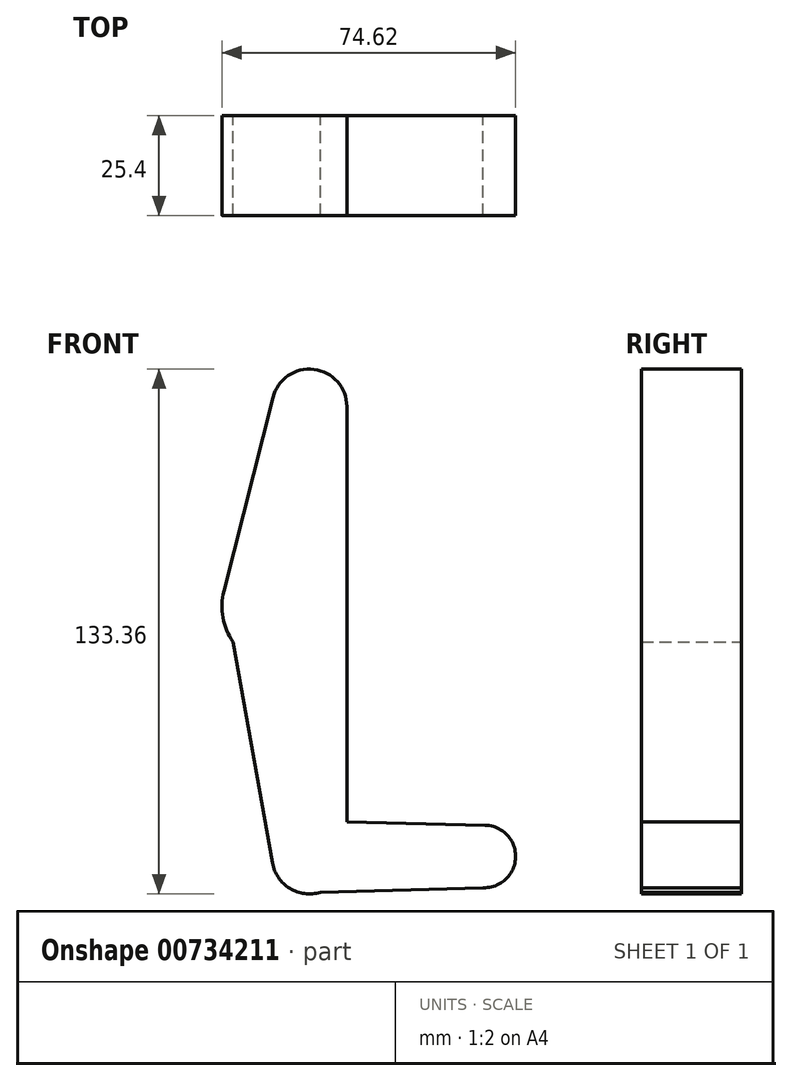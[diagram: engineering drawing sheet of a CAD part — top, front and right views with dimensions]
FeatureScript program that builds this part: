
annotation { "Feature Type Name" : "Feature", "Feature Type Description" : "" }
export const myFeature = defineFeature(function(context is Context, id is Id, definition is map)
    precondition{}
    {
        {
            var Q0;
            Q0=qCreatedBy(makeId("Front.planeOp"),FACE);
            var sketch = newSketch(context, id + "F0", { "sketchPlane" : qUnion([Q0])});
            skPoint(sketch, "E0.end.orphan", {"position": v(0, 1423.13) * mm});
            skLineSegment(sketch, "E1", {"start": v(0, 0) * mm, "end": v(44.45, 0) * mm});
            skCircle(sketch, "E2", {"center": v(0, 114.3) * mm, "radius": 9.53 * mm});
            skCircle(sketch, "E3", {"center": v(-6.35, 63.5) * mm, "radius": 15.88 * mm});
            skCircle(sketch, "E4", {"center": v(44.45, 0) * mm, "radius": 7.94 * mm});
            skCircle(sketch, "E5", {"center": v(0, 0) * mm, "radius": 9.53 * mm});
            skLineSegment(sketch, "E6", {"start": v(0, 114.3) * mm, "end": v(0, 0) * mm, "construction": true});
            skLineSegment(sketch, "E7", {"start": v(-9.25, 116.57) * mm, "end": v(-21.74, 67.4) * mm});
            skLineSegment(sketch, "E8", {"start": v(-21.74, 67.4) * mm, "end": v(-9.38, -1.68) * mm});
            skLineSegment(sketch, "E9", {"start": v(3.4, 8.9) * mm, "end": v(44.63, 7.94) * mm});
            skLineSegment(sketch, "E10", {"start": v(45.2, -7.9) * mm, "end": v(2.8, -9.1) * mm});
            skLineSegment(sketch, "E11", {"start": v(9.5, 113.7) * mm, "end": v(9.52, 114.3) * mm});
            skPoint(sketch, "E12.start.orphan", {"position": v(9.1, 59.85) * mm});
            skPoint(sketch, "E13.end.orphan", {"position": v(7.85, 59.85) * mm});
            skLineSegment(sketch, "E14", {"start": v(9.52, 114.3) * mm, "end": v(9.5, 113.57) * mm});
            skPoint(sketch, "E15.end.orphan", {"position": v(7.85, 70.6) * mm});
            skLineSegment(sketch, "E16", {"start": v(9.52, 0) * mm, "end": v(9.52, 70.6) * mm});
            skLineSegment(sketch, "E17", {"start": v(9.52, 70.6) * mm, "end": v(9.52, 114.3) * mm});
            skSolve(sketch);
        }
        {
            var Q0;
            Q0 = qSketchRegion(id + "F0", true);
            extrude(context, id + "F1", {"entities" : qUnion([Q0]), "depth" : 25.4 * mm, "offsetDistance" : 25.4 * mm});
        }
    });
